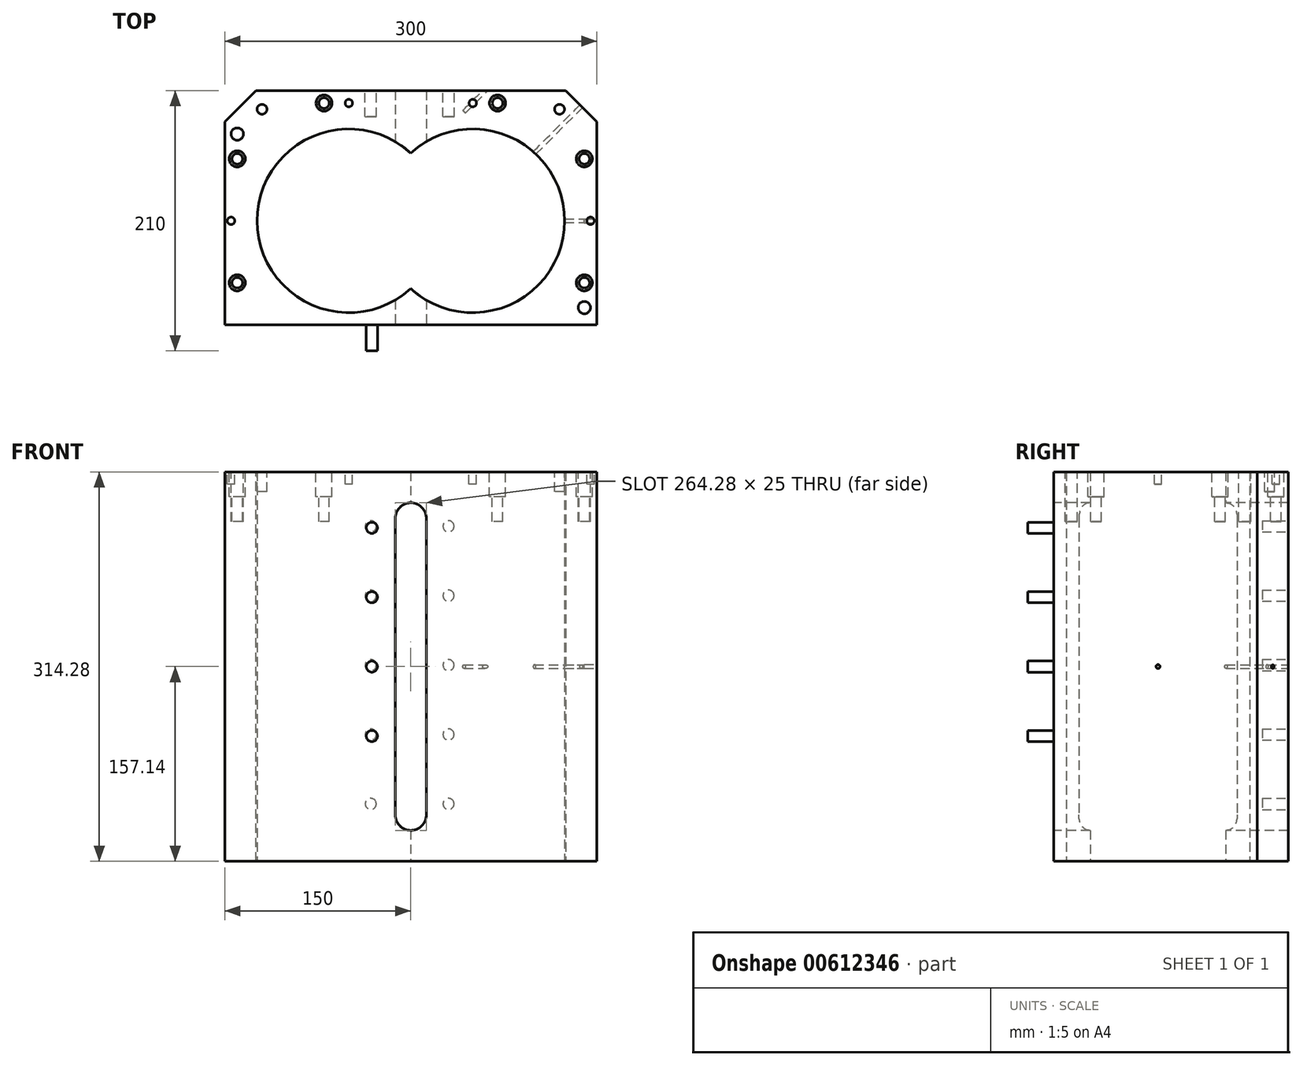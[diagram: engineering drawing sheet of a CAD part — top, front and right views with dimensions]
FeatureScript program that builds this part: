
annotation { "Feature Type Name" : "Feature", "Feature Type Description" : "" }
export const myFeature = defineFeature(function(context is Context, id is Id, definition is map)
    precondition{}
    {
        {
            var Q0;
            Q0=qCreatedBy(makeId("Top.planeOp"),FACE);
            var sketch = newSketch(context, id + "F0", { "sketchPlane" : qUnion([Q0])});
            skLineSegment(sketch, "E0.top", {"start": v(-150, 105) * mm, "end": v(150, 105) * mm});
            skLineSegment(sketch, "E0.right", {"start": v(150, -105) * mm, "end": v(150, 105) * mm});
            skArc(sketch, "E1", {"start": v(-50, 81) * mm, "mid": v(-131, 0) * mm, "end": v(-50, -81) * mm});
            skArc(sketch, "E2", {"start": v(50, -81) * mm, "mid": v(131, 0) * mm, "end": v(50, 81) * mm});
            skArc(sketch, "E3", {"start": v(-50, 86) * mm, "mid": v(-136, 0) * mm, "end": v(-50, -86) * mm});
            skArc(sketch, "E4", {"start": v(0, 54.66) * mm, "mid": v(-124.08, 0) * mm, "end": v(0, -54.66) * mm});
            skArc(sketch, "E5", {"start": v(50, -86) * mm, "mid": v(136, 0) * mm, "end": v(50, 86) * mm});
            skArc(sketch, "E6", {"start": v(0, -54.66) * mm, "mid": v(124.08, 0) * mm, "end": v(0, 54.66) * mm});
            skLineSegment(sketch, "E7", {"start": v(-50, -81) * mm, "end": v(50, -81) * mm});
            skLineSegment(sketch, "E8", {"start": v(-50, 81) * mm, "end": v(50, 81) * mm});
            skLineSegment(sketch, "E9", {"start": v(-50, 86) * mm, "end": v(50, 86) * mm});
            skLineSegment(sketch, "E10", {"start": v(50, -86) * mm, "end": v(-50, -86) * mm});
            skLineSegment(sketch, "E11", {"start": v(-150, 105) * mm, "end": v(-150, -105) * mm});
            skLineSegment(sketch, "E12", {"start": v(-150, -105) * mm, "end": v(150, -105) * mm});
            skSolve(sketch);
        }
        {
            var Q0;
            Q0=makeQuery(id+"F0.imprint","IMPRINT",FACE,{"disambiguationData":[TD([[makeQuery(id+"F0.imprint","IMPRINT",EDGE,{"derivedFrom":sQuery(id+"F0.wireOp",EDGE,"E0.top")}),-1.0]])]});
            var Q1;
            Q1=makeQuery(id+"F0.imprint","IMPRINT",FACE,{"disambiguationData":[TD([[makeQuery(id+"F0.imprint","IMPRINT",EDGE,{"derivedFrom":sQuery(id+"F0.wireOp",EDGE,"E1")}),-1.0]])]});
            var Q2;
            Q2=makeQuery(id+"F0.imprint","IMPRINT",FACE,{"disambiguationData":[TD([[makeQuery(id+"F0.imprint","IMPRINT",EDGE,{"derivedFrom":sQuery(id+"F0.wireOp",EDGE,"E1")}),1.0]])]});
            extrude(context, id + "F1", {"entities" : qUnion([Q0, Q1, Q2]), "depth" : 157.14 * mm, "offsetDistance" : 25 * mm, "hasSecondDirection" : true, "secondDirectionOppositeDirection" : true, "secondDirectionDepth" : 157.14 * mm});
        }
        {
            var Q0;
            Q0=qCreatedBy(makeId("Front.planeOp"),FACE);
            var sketch = newSketch(context, id + "F2", { "sketchPlane" : qUnion([Q0])});
            skLineSegment(sketch, "E13.left", {"start": v(-12.5, 119.64) * mm, "end": v(-12.5, -119.64) * mm});
            skLineSegment(sketch, "E13.right", {"start": v(12.5, 119.64) * mm, "end": v(12.5, -119.64) * mm});
            skArc(sketch, "E14", {"start": v(12.5, 119.64) * mm, "mid": v(0, 132.14) * mm, "end": v(-12.5, 119.64) * mm});
            skArc(sketch, "E15", {"start": v(-12.5, -119.64) * mm, "mid": v(0, -132.14) * mm, "end": v(12.5, -119.64) * mm});
            skSolve(sketch);
        }
        {
            var Q0;
            Q0=makeQuery(id+"F2.imprint","IMPRINT",FACE,{"disambiguationData":[TD([[makeQuery(id+"F2.imprint","IMPRINT",EDGE,{"derivedFrom":sQuery(id+"F2.wireOp",EDGE,"E13.left")}),1.0]])]});
            extrude(context, id + "F3", {"entities" : qUnion([Q0]), "operationType" : NewBodyOperationType.REMOVE, "oppositeDirection" : true, "depth" : 105 * mm, "offsetDistance" : 25 * mm, "hasSecondDirection" : true, "secondDirectionOppositeDirection" : false, "secondDirectionDepth" : 105 * mm});
        }
        {
            var Q0;
            Q0=makeQuery(id+"F1.opExtrude","SWEPT_FACE",FACE,{"disambiguationData":[OSD([sQuery(id+"F0.wireOp",EDGE,"E12")])]});
            var sketch = newSketch(context, id + "F4", { "sketchPlane" : qUnion([Q0])});
            skCircle(sketch, "E16", {"center": v(31.4, -112) * mm, "radius": 4.5 * mm});
            skCircle(sketch, "E17.3.0", {"center": v(-31.4, -112) * mm, "radius": 4.5 * mm});
            skCircle(sketch, "E18", {"center": v(31.4, -56) * mm, "radius": 4.5 * mm});
            skCircle(sketch, "E19", {"center": v(31.4, 0) * mm, "radius": 4.5 * mm});
            skCircle(sketch, "E20", {"center": v(31.4, 56) * mm, "radius": 4.5 * mm});
            skCircle(sketch, "E21", {"center": v(31.4, 112) * mm, "radius": 4.5 * mm});
            skCircle(sketch, "E22.MirrorC", {"center": v(-31.4, 112) * mm, "radius": 4.5 * mm});
            skCircle(sketch, "E23.MirrorC", {"center": v(-31.4, 56) * mm, "radius": 4.5 * mm});
            skCircle(sketch, "E24.MirrorC", {"center": v(-31.4, 0) * mm, "radius": 4.5 * mm});
            skCircle(sketch, "E25.MirrorC", {"center": v(-31.4, -56) * mm, "radius": 4.5 * mm});
            skSolve(sketch);
        }
        {
            var Q0;
            Q0=makeQuery(id+"F4.imprint","IMPRINT",FACE,{"disambiguationData":[TD([[makeQuery(id+"F4.imprint","IMPRINT",EDGE,{"derivedFrom":sQuery(id+"F4.wireOp",EDGE,"d7dd9468-2d27-4aad-933e-c1cbb9862e0e0.MirrorC")}),-1.0]])]});
            var Q1;
            Q1=makeQuery(id+"F4.imprint","IMPRINT",FACE,{"disambiguationData":[TD([[makeQuery(id+"F4.imprint","IMPRINT",EDGE,{"derivedFrom":sQuery(id+"F4.wireOp",EDGE,"e4527831-351d-4cbc-a9db-844e189b8d3e0.MirrorC")}),-1.0]])]});
            var Q2;
            Q2=makeQuery(id+"F4.imprint","IMPRINT",FACE,{"disambiguationData":[TD([[makeQuery(id+"F4.imprint","IMPRINT",EDGE,{"derivedFrom":sQuery(id+"F4.wireOp",EDGE,"fd657ee0-c63a-4506-9bfe-7fd184a3cc340.MirrorC")}),-1.0]])]});
            var Q3;
            Q3=makeQuery(id+"F4.imprint","IMPRINT",FACE,{"disambiguationData":[TD([[makeQuery(id+"F4.imprint","IMPRINT",EDGE,{"derivedFrom":sQuery(id+"F4.wireOp",EDGE,"E22.MirrorC")}),-1.0]])]});
            var Q4;
            Q4=makeQuery(id+"F4.imprint","IMPRINT",FACE,{"disambiguationData":[TD([[makeQuery(id+"F4.imprint","IMPRINT",EDGE,{"derivedFrom":sQuery(id+"F4.wireOp",EDGE,"E23.MirrorC")}),-1.0]])]});
            var Q5;
            Q5=makeQuery(id+"F4.imprint","IMPRINT",FACE,{"disambiguationData":[TD([[makeQuery(id+"F4.imprint","IMPRINT",EDGE,{"derivedFrom":sQuery(id+"F4.wireOp",EDGE,"E24.MirrorC")}),-1.0]])]});
            var Q6;
            Q6=makeQuery(id+"F4.imprint","IMPRINT",FACE,{"disambiguationData":[TD([[makeQuery(id+"F4.imprint","IMPRINT",EDGE,{"derivedFrom":sQuery(id+"F4.wireOp",EDGE,"E25.MirrorC")}),-1.0]])]});
            var Q7;
            Q7=makeQuery(id+"F4.imprint","IMPRINT",FACE,{"disambiguationData":[TD([[makeQuery(id+"F4.imprint","IMPRINT",EDGE,{"derivedFrom":sQuery(id+"F4.wireOp",EDGE,"E17.3.0")}),1.0]])]});
            var Q8;
            Q8=makeQuery(id+"F4.imprint","IMPRINT",FACE,{"disambiguationData":[TD([[makeQuery(id+"F4.imprint","IMPRINT",EDGE,{"derivedFrom":sQuery(id+"F4.wireOp",EDGE,"E16")}),1.0]])]});
            var Q9;
            Q9=makeQuery(id+"F4.imprint","IMPRINT",FACE,{"disambiguationData":[TD([[makeQuery(id+"F4.imprint","IMPRINT",EDGE,{"derivedFrom":sQuery(id+"F4.wireOp",EDGE,"E18")}),1.0]])]});
            var Q10;
            Q10=makeQuery(id+"F4.imprint","IMPRINT",FACE,{"disambiguationData":[TD([[makeQuery(id+"F4.imprint","IMPRINT",EDGE,{"derivedFrom":sQuery(id+"F4.wireOp",EDGE,"E19")}),1.0]])]});
            var Q11;
            Q11=makeQuery(id+"F4.imprint","IMPRINT",FACE,{"disambiguationData":[TD([[makeQuery(id+"F4.imprint","IMPRINT",EDGE,{"derivedFrom":sQuery(id+"F4.wireOp",EDGE,"E20")}),1.0]])]});
            var Q12;
            Q12=makeQuery(id+"F4.imprint","IMPRINT",FACE,{"disambiguationData":[TD([[makeQuery(id+"F4.imprint","IMPRINT",EDGE,{"derivedFrom":sQuery(id+"F4.wireOp",EDGE,"E21")}),1.0]])]});
            var Q13;
            Q13=makeQuery(id+"F4.imprint","IMPRINT",FACE,{"disambiguationData":[TD([[makeQuery(id+"F4.imprint","IMPRINT",EDGE,{"derivedFrom":sQuery(id+"F4.wireOp",EDGE,"9xouMa0X-Z2gg-Zd0Z-shEU-6vQGR6SH1V26")}),1.0]])]});
            var Q14;
            Q14=makeQuery(id+"F4.imprint","IMPRINT",FACE,{"disambiguationData":[TD([[makeQuery(id+"F4.imprint","IMPRINT",EDGE,{"derivedFrom":sQuery(id+"F4.wireOp",EDGE,"f3L94pXb-UXOi-ypgG-wCGD-cI5cRXITr2G3")}),1.0]])]});
            var Q15;
            Q15=makeQuery(id+"F4.imprint","IMPRINT",FACE,{"disambiguationData":[TD([[makeQuery(id+"F4.imprint","IMPRINT",EDGE,{"derivedFrom":sQuery(id+"F4.wireOp",EDGE,"yZ0yZw9I-iKcT-nnKl-4C5n-boTp4ZFd5wa9")}),1.0]])]});
            extrude(context, id + "F5", {"entities" : qUnion([Q0, Q1, Q2, Q3, Q4, Q5, Q6, Q7, Q8, Q9, Q10, Q11, Q12, Q13, Q14, Q15]), "operationType" : NewBodyOperationType.REMOVE, "oppositeDirection" : true, "depth" : 21 * mm, "offsetDistance" : 25 * mm});
        }
        {
            var Q0;
            Q0=makeQuery(id+"F1.opExtrude","CAP_FACE",FACE,{"disambiguationData":[OSD([sQuery(id+"F0.wireOp",EDGE,"E0.top"),sQuery(id+"F0.wireOp",EDGE,"E0.right"),sQuery(id+"F0.wireOp",EDGE,"E3"),sQuery(id+"F0.wireOp",EDGE,"E5"),sQuery(id+"F0.wireOp",EDGE,"E9"),sQuery(id+"F0.wireOp",EDGE,"E10"),sQuery(id+"F0.wireOp",EDGE,"E11"),sQuery(id+"F0.wireOp",EDGE,"E12")])],"isStart":false});
            var sketch = newSketch(context, id + "F6", { "sketchPlane" : qUnion([Q0])});
            skCircle(sketch, "E26", {"center": v(-70, 95) * mm, "radius": 6.5 * mm});
            skCircle(sketch, "E27", {"center": v(70, 95) * mm, "radius": 6.5 * mm});
            skCircle(sketch, "E28", {"center": v(70, -95) * mm, "radius": 6.5 * mm});
            skCircle(sketch, "E29", {"center": v(-70, -95) * mm, "radius": 6.5 * mm});
            skCircle(sketch, "E30", {"center": v(-140, -50) * mm, "radius": 6.5 * mm});
            skCircle(sketch, "E31", {"center": v(-140, 50) * mm, "radius": 6.5 * mm});
            skCircle(sketch, "E32", {"center": v(140, 50) * mm, "radius": 6.5 * mm});
            skCircle(sketch, "E33", {"center": v(140, -50) * mm, "radius": 6.5 * mm});
            skCircle(sketch, "E34", {"center": v(-140, 70) * mm, "radius": 5 * mm});
            skCircle(sketch, "E35", {"center": v(140, -70) * mm, "radius": 5 * mm});
            skCircle(sketch, "E36", {"center": v(-145, 0) * mm, "radius": 3 * mm});
            skCircle(sketch, "E37", {"center": v(145, 0) * mm, "radius": 3 * mm});
            skCircle(sketch, "E38", {"center": v(50, -95) * mm, "radius": 3 * mm});
            skCircle(sketch, "E39", {"center": v(-50, -95) * mm, "radius": 3 * mm});
            skCircle(sketch, "E40", {"center": v(-50, 95) * mm, "radius": 3 * mm});
            skCircle(sketch, "E41", {"center": v(50, 95) * mm, "radius": 3 * mm});
            skCircle(sketch, "E42", {"center": v(-120, 90) * mm, "radius": 4 * mm});
            skCircle(sketch, "E43", {"center": v(-120, -90) * mm, "radius": 4 * mm});
            skCircle(sketch, "E44", {"center": v(120, -90) * mm, "radius": 4 * mm});
            skCircle(sketch, "E45", {"center": v(120, 90) * mm, "radius": 4 * mm});
            skCircle(sketch, "E46", {"center": v(-70, 95) * mm, "radius": 4.25 * mm});
            skCircle(sketch, "E47", {"center": v(70, 95) * mm, "radius": 4.25 * mm});
            skCircle(sketch, "E48", {"center": v(140, 50) * mm, "radius": 4.25 * mm});
            skCircle(sketch, "E49", {"center": v(140, -50) * mm, "radius": 4.25 * mm});
            skCircle(sketch, "E50", {"center": v(70, -95) * mm, "radius": 4.25 * mm});
            skCircle(sketch, "E51", {"center": v(-70, -95) * mm, "radius": 4.25 * mm});
            skCircle(sketch, "E52", {"center": v(-140, -50) * mm, "radius": 4.25 * mm});
            skCircle(sketch, "E53", {"center": v(-140, 50) * mm, "radius": 4.25 * mm});
            skSolve(sketch);
        }
        {
            var Q0;
            Q0=makeQuery(id+"F6.imprint","IMPRINT",FACE,{"disambiguationData":[TD([[makeQuery(id+"F6.imprint","IMPRINT",EDGE,{"derivedFrom":sQuery(id+"F6.wireOp",EDGE,"E32")}),1.0]])]});
            var Q1;
            Q1=makeQuery(id+"F6.imprint","IMPRINT",FACE,{"disambiguationData":[TD([[makeQuery(id+"F6.imprint","IMPRINT",EDGE,{"derivedFrom":sQuery(id+"F6.wireOp",EDGE,"E33")}),1.0]])]});
            var Q2;
            Q2=makeQuery(id+"F6.imprint","IMPRINT",FACE,{"disambiguationData":[TD([[makeQuery(id+"F6.imprint","IMPRINT",EDGE,{"derivedFrom":sQuery(id+"F6.wireOp",EDGE,"E28")}),1.0]])]});
            var Q3;
            Q3=makeQuery(id+"F6.imprint","IMPRINT",FACE,{"disambiguationData":[TD([[makeQuery(id+"F6.imprint","IMPRINT",EDGE,{"derivedFrom":sQuery(id+"F6.wireOp",EDGE,"E29")}),1.0]])]});
            var Q4;
            Q4=makeQuery(id+"F6.imprint","IMPRINT",FACE,{"disambiguationData":[TD([[makeQuery(id+"F6.imprint","IMPRINT",EDGE,{"derivedFrom":sQuery(id+"F6.wireOp",EDGE,"E30")}),1.0]])]});
            var Q5;
            Q5=makeQuery(id+"F6.imprint","IMPRINT",FACE,{"disambiguationData":[TD([[makeQuery(id+"F6.imprint","IMPRINT",EDGE,{"derivedFrom":sQuery(id+"F6.wireOp",EDGE,"E31")}),1.0]])]});
            var Q6;
            Q6=makeQuery(id+"F6.imprint","IMPRINT",FACE,{"disambiguationData":[TD([[makeQuery(id+"F6.imprint","IMPRINT",EDGE,{"derivedFrom":sQuery(id+"F6.wireOp",EDGE,"E26")}),1.0]])]});
            var Q7;
            Q7=makeQuery(id+"F6.imprint","IMPRINT",FACE,{"disambiguationData":[TD([[makeQuery(id+"F6.imprint","IMPRINT",EDGE,{"derivedFrom":sQuery(id+"F6.wireOp",EDGE,"E27")}),1.0]])]});
            extrude(context, id + "F7", {"entities" : qUnion([Q0, Q1, Q2, Q3, Q4, Q5, Q6, Q7]), "operationType" : NewBodyOperationType.REMOVE, "oppositeDirection" : true, "depth" : 20 * mm, "offsetDistance" : 25 * mm});
        }
        {
            var Q0;
            Q0=makeQuery(id+"F6.imprint","IMPRINT",FACE,{"disambiguationData":[TD([[makeQuery(id+"F6.imprint","IMPRINT",EDGE,{"derivedFrom":sQuery(id+"F6.wireOp",EDGE,"E40")}),1.0]])]});
            var Q1;
            Q1=makeQuery(id+"F6.imprint","IMPRINT",FACE,{"disambiguationData":[TD([[makeQuery(id+"F6.imprint","IMPRINT",EDGE,{"derivedFrom":sQuery(id+"F6.wireOp",EDGE,"E36")}),1.0]])]});
            var Q2;
            Q2=makeQuery(id+"F6.imprint","IMPRINT",FACE,{"disambiguationData":[TD([[makeQuery(id+"F6.imprint","IMPRINT",EDGE,{"derivedFrom":sQuery(id+"F6.wireOp",EDGE,"E41")}),1.0]])]});
            var Q3;
            Q3=makeQuery(id+"F6.imprint","IMPRINT",FACE,{"disambiguationData":[TD([[makeQuery(id+"F6.imprint","IMPRINT",EDGE,{"derivedFrom":sQuery(id+"F6.wireOp",EDGE,"E37")}),1.0]])]});
            var Q4;
            Q4=makeQuery(id+"F6.imprint","IMPRINT",FACE,{"disambiguationData":[TD([[makeQuery(id+"F6.imprint","IMPRINT",EDGE,{"derivedFrom":sQuery(id+"F6.wireOp",EDGE,"E39")}),1.0]])]});
            var Q5;
            Q5=makeQuery(id+"F6.imprint","IMPRINT",FACE,{"disambiguationData":[TD([[makeQuery(id+"F6.imprint","IMPRINT",EDGE,{"derivedFrom":sQuery(id+"F6.wireOp",EDGE,"E38")}),1.0]])]});
            extrude(context, id + "F8", {"entities" : qUnion([Q0, Q1, Q2, Q3, Q4, Q5]), "operationType" : NewBodyOperationType.REMOVE, "oppositeDirection" : true, "depth" : 10 * mm, "offsetDistance" : 25 * mm});
        }
        {
            var Q0;
            Q0=makeQuery(id+"F6.imprint","IMPRINT",FACE,{"disambiguationData":[TD([[makeQuery(id+"F6.imprint","IMPRINT",EDGE,{"derivedFrom":sQuery(id+"F6.wireOp",EDGE,"E46")}),1.0]])]});
            var Q1;
            Q1=makeQuery(id+"F6.imprint","IMPRINT",FACE,{"disambiguationData":[TD([[makeQuery(id+"F6.imprint","IMPRINT",EDGE,{"derivedFrom":sQuery(id+"F6.wireOp",EDGE,"E53")}),1.0]])]});
            var Q2;
            Q2=makeQuery(id+"F6.imprint","IMPRINT",FACE,{"disambiguationData":[TD([[makeQuery(id+"F6.imprint","IMPRINT",EDGE,{"derivedFrom":sQuery(id+"F6.wireOp",EDGE,"E52")}),1.0]])]});
            var Q3;
            Q3=makeQuery(id+"F6.imprint","IMPRINT",FACE,{"disambiguationData":[TD([[makeQuery(id+"F6.imprint","IMPRINT",EDGE,{"derivedFrom":sQuery(id+"F6.wireOp",EDGE,"E51")}),1.0]])]});
            var Q4;
            Q4=makeQuery(id+"F6.imprint","IMPRINT",FACE,{"disambiguationData":[TD([[makeQuery(id+"F6.imprint","IMPRINT",EDGE,{"derivedFrom":sQuery(id+"F6.wireOp",EDGE,"E50")}),1.0]])]});
            var Q5;
            Q5=makeQuery(id+"F6.imprint","IMPRINT",FACE,{"disambiguationData":[TD([[makeQuery(id+"F6.imprint","IMPRINT",EDGE,{"derivedFrom":sQuery(id+"F6.wireOp",EDGE,"E49")}),1.0]])]});
            var Q6;
            Q6=makeQuery(id+"F6.imprint","IMPRINT",FACE,{"disambiguationData":[TD([[makeQuery(id+"F6.imprint","IMPRINT",EDGE,{"derivedFrom":sQuery(id+"F6.wireOp",EDGE,"E48")}),1.0]])]});
            var Q7;
            Q7=makeQuery(id+"F6.imprint","IMPRINT",FACE,{"disambiguationData":[TD([[makeQuery(id+"F6.imprint","IMPRINT",EDGE,{"derivedFrom":sQuery(id+"F6.wireOp",EDGE,"E47")}),1.0]])]});
            var Q8;
            Q8=makeQuery(id+"F6.imprint","IMPRINT",FACE,{"disambiguationData":[TD([[makeQuery(id+"F6.imprint","IMPRINT",EDGE,{"derivedFrom":sQuery(id+"F6.wireOp",EDGE,"E34")}),1.0]])]});
            var Q9;
            Q9=makeQuery(id+"F6.imprint","IMPRINT",FACE,{"disambiguationData":[TD([[makeQuery(id+"F6.imprint","IMPRINT",EDGE,{"derivedFrom":sQuery(id+"F6.wireOp",EDGE,"E35")}),1.0]])]});
            extrude(context, id + "F9", {"entities" : qUnion([Q0, Q1, Q2, Q3, Q4, Q5, Q6, Q7, Q8, Q9]), "operationType" : NewBodyOperationType.REMOVE, "oppositeDirection" : true, "depth" : 40 * mm, "offsetDistance" : 25 * mm});
        }
        {
            var Q0;
            Q0=makeQuery(id+"F6.imprint","IMPRINT",FACE,{"disambiguationData":[TD([[makeQuery(id+"F6.imprint","IMPRINT",EDGE,{"derivedFrom":sQuery(id+"F6.wireOp",EDGE,"E42")}),1.0]])]});
            var Q1;
            Q1=makeQuery(id+"F6.imprint","IMPRINT",FACE,{"disambiguationData":[TD([[makeQuery(id+"F6.imprint","IMPRINT",EDGE,{"derivedFrom":sQuery(id+"F6.wireOp",EDGE,"E43")}),1.0]])]});
            var Q2;
            Q2=makeQuery(id+"F6.imprint","IMPRINT",FACE,{"disambiguationData":[TD([[makeQuery(id+"F6.imprint","IMPRINT",EDGE,{"derivedFrom":sQuery(id+"F6.wireOp",EDGE,"E44")}),1.0]])]});
            var Q3;
            Q3=makeQuery(id+"F6.imprint","IMPRINT",FACE,{"disambiguationData":[TD([[makeQuery(id+"F6.imprint","IMPRINT",EDGE,{"derivedFrom":sQuery(id+"F6.wireOp",EDGE,"E45")}),1.0]])]});
            extrude(context, id + "F10", {"entities" : qUnion([Q0, Q1, Q2, Q3]), "operationType" : NewBodyOperationType.REMOVE, "oppositeDirection" : true, "depth" : 16 * mm, "offsetDistance" : 25 * mm});
        }
        {
            var Q0;
            Q0=makeQuery(id+"F1.opExtrude","SWEPT_EDGE",EDGE,{"disambiguationData":[OSD([sQuery(id+"F0.wireOp",EDGE,"E0.top"),sQuery(id+"F0.wireOp",EDGE,"E11")])]});
            var Q1;
            Q1=makeQuery(id+"F1.opExtrude","SWEPT_EDGE",EDGE,{"disambiguationData":[OSD([sQuery(id+"F0.wireOp",EDGE,"E11"),sQuery(id+"F0.wireOp",EDGE,"E12")])]});
            var Q2;
            Q2=makeQuery(id+"F1.opExtrude","SWEPT_EDGE",EDGE,{"disambiguationData":[OSD([sQuery(id+"F0.wireOp",EDGE,"E0.top"),sQuery(id+"F0.wireOp",EDGE,"E0.right")])]});
            var Q3;
            Q3=makeQuery(id+"F1.opExtrude","SWEPT_EDGE",EDGE,{"disambiguationData":[OSD([sQuery(id+"F0.wireOp",EDGE,"E0.right"),sQuery(id+"F0.wireOp",EDGE,"E12")])]});
            chamfer(context, id + "F11", {"entities" : qUnion([Q0, Q1, Q2, Q3]), "width" : 25 * mm, "tangentPropagation" : true});
        }
        {
            var Q0;
            Q0=makeQuery(id+"F1.opExtrude","SWEPT_FACE",FACE,{"disambiguationData":[OSD([sQuery(id+"F0.wireOp",EDGE,"E0.right")])]});
            var sketch = newSketch(context, id + "F12", { "sketchPlane" : qUnion([Q0])});
            skCircle(sketch, "E54", {"center": v(0, 0) * mm, "radius": 1.59 * mm});
            skCircle(sketch, "E55", {"center": v(0, 0) * mm, "radius": 1.5 * mm});
            skSolve(sketch);
        }
        {
            var Q0;
            Q0=makeQuery(id+"F12.imprint","IMPRINT",FACE,{"disambiguationData":[TD([[makeQuery(id+"F12.imprint","IMPRINT",EDGE,{"derivedFrom":sQuery(id+"F12.wireOp",EDGE,"E54")}),1.0]])]});
            extrude(context, id + "F13", {"entities" : qUnion([Q0]), "operationType" : NewBodyOperationType.REMOVE, "oppositeDirection" : true, "depth" : 10 * mm, "offsetDistance" : 25 * mm});
        }
        {
            var Q0;
            Q0=makeQuery(id+"F13.boolean.opBoolean","SPLIT",FACE,{"disambiguationData":[TD([makeQuery(id+"F13.opExtrude","SWEPT_FACE",FACE,{"disambiguationData":[OSD([sQuery(id+"F12.wireOp",EDGE,"E55")])]})])],"derivedFrom":makeQuery(id+"F1.opExtrude","SWEPT_FACE",FACE,{"disambiguationData":[OSD([sQuery(id+"F0.wireOp",EDGE,"E0.right")])]})});
            extrude(context, id + "F14", {"entities" : qUnion([Q0]), "operationType" : NewBodyOperationType.REMOVE, "oppositeDirection" : true, "depth" : 40 * mm, "offsetDistance" : 25 * mm});
        }
        {
            var Q0;
            Q0=makeQuery(id+"F11.opChamfer","BLEND_FACE",FACE,{"disambiguationData":[OSD([sQuery(id+"F0.wireOp",EDGE,"E0.right"),sQuery(id+"F0.wireOp",EDGE,"E12")])]});
            var sketch = newSketch(context, id + "F15", { "sketchPlane" : qUnion([Q0])});
            skCircle(sketch, "E56", {"center": v(31.82, 0) * mm, "radius": 1.59 * mm});
            skCircle(sketch, "E57", {"center": v(31.82, 0) * mm, "radius": 1.5 * mm});
            skSolve(sketch);
        }
        {
            var Q0;
            Q0=makeQuery(id+"F15.imprint","IMPRINT",FACE,{"disambiguationData":[TD([[makeQuery(id+"F15.imprint","IMPRINT",EDGE,{"derivedFrom":sQuery(id+"F15.wireOp",EDGE,"E57")}),1.0]])]});
            extrude(context, id + "F16", {"entities" : qUnion([Q0]), "operationType" : NewBodyOperationType.REMOVE, "oppositeDirection" : true, "depth" : 70 * mm, "offsetDistance" : 25 * mm});
        }
        {
            var Q0;
            Q0=makeQuery(id+"F11.opChamfer","BLEND_FACE",FACE,{"disambiguationData":[OSD([sQuery(id+"F0.wireOp",EDGE,"E0.top"),sQuery(id+"F0.wireOp",EDGE,"E0.right")])]});
            var sketch = newSketch(context, id + "F17", { "sketchPlane" : qUnion([Q0])});
            skCircle(sketch, "E58", {"center": v(-31.82, 0) * mm, "radius": 1.59 * mm});
            skCircle(sketch, "E59", {"center": v(-31.82, 0) * mm, "radius": 1.5 * mm});
            skSolve(sketch);
        }
        {
            var Q0;
            Q0=makeQuery(id+"F17.imprint","IMPRINT",FACE,{"disambiguationData":[TD([[makeQuery(id+"F17.imprint","IMPRINT",EDGE,{"derivedFrom":sQuery(id+"F17.wireOp",EDGE,"E59")}),1.0]])]});
            extrude(context, id + "F18", {"entities" : qUnion([Q0]), "operationType" : NewBodyOperationType.REMOVE, "oppositeDirection" : true, "depth" : 70 * mm, "offsetDistance" : 25 * mm});
        }
        {
            var Q0;
            {var subQ0=sQuery(id+"F0.wireOp",EDGE,"E0.top");var subQ1=sQuery(id+"F0.wireOp",EDGE,"E12");var subQ2=sQuery(id+"F0.wireOp",EDGE,"E11");var subQ3=sQuery(id+"F0.wireOp",EDGE,"E0.right");var subQ4=sQuery(id+"F0.wireOp",EDGE,"E6");var subQ5=sQuery(id+"F0.wireOp",EDGE,"E4");Q0=makeQuery(id+"F7.boolean.opBoolean","SPLIT",FACE,{"disambiguationData":[TD([makeQuery(id+"F1.opExtrude","SWEPT_FACE",FACE,{"disambiguationData":[OSD([subQ0])]})])],"derivedFrom":makeQuery(id+"F1.opExtrude","CAP_FACE",FACE,{"disambiguationData":[OSD([subQ0,subQ3,subQ5,subQ4,subQ2,subQ1])],"isStart":false})});}
            var sketch = newSketch(context, id + "F19", { "sketchPlane" : qUnion([Q0])});
            skArc(sketch, "E60", {"start": v(50, -86) * mm, "mid": v(136, 0) * mm, "end": v(50, 86) * mm});
            skArc(sketch, "E61", {"start": v(50, -81) * mm, "mid": v(131, 0) * mm, "end": v(50, 81) * mm});
            skArc(sketch, "E62", {"start": v(-50, 86) * mm, "mid": v(-136, 0) * mm, "end": v(-50, -86) * mm});
            skArc(sketch, "E63", {"start": v(-50, 81) * mm, "mid": v(-131, 0) * mm, "end": v(-50, -81) * mm});
            skLineSegment(sketch, "E64", {"start": v(-50, 86) * mm, "end": v(50, 86) * mm});
            skLineSegment(sketch, "E65", {"start": v(50, 81) * mm, "end": v(-50, 81) * mm});
            skLineSegment(sketch, "E66", {"start": v(-50, -81) * mm, "end": v(50, -81) * mm});
            skLineSegment(sketch, "E67", {"start": v(50, -86) * mm, "end": v(-50, -86) * mm});
            skSolve(sketch);
        }
        {
            var Q0;
            Q0=makeQuery(id+"F19.imprint","IMPRINT",FACE,{"disambiguationData":[TD([[makeQuery(id+"F19.imprint","IMPRINT",EDGE,{"derivedFrom":sQuery(id+"F19.wireOp",EDGE,"E60")}),1.0]])]});
            extrude(context, id + "F20", {"entities" : qUnion([Q0]), "operationType" : NewBodyOperationType.REMOVE, "oppositeDirection" : true, "depth" : 2.7 * mm, "offsetDistance" : 25 * mm});
        }
        {
            var Q0;
            Q0=makeQuery(id+"F1.opExtrude","CAP_FACE",FACE,{"disambiguationData":[OSD([sQuery(id+"F0.wireOp",EDGE,"E0.top"),sQuery(id+"F0.wireOp",EDGE,"E0.right"),sQuery(id+"F0.wireOp",EDGE,"E4"),sQuery(id+"F0.wireOp",EDGE,"E6"),sQuery(id+"F0.wireOp",EDGE,"E11"),sQuery(id+"F0.wireOp",EDGE,"E12")])],"isStart":true});
            var sketch = newSketch(context, id + "F21", { "sketchPlane" : qUnion([Q0])});
            skArc(sketch, "E68", {"start": v(-50, 86) * mm, "mid": v(-136, 0) * mm, "end": v(-50, -86) * mm});
            skArc(sketch, "E69", {"start": v(-50, 81) * mm, "mid": v(-131, 0) * mm, "end": v(-50, -81) * mm});
            skArc(sketch, "E70", {"start": v(50, -86) * mm, "mid": v(136, 0) * mm, "end": v(50, 86) * mm});
            skArc(sketch, "E71", {"start": v(50, -81) * mm, "mid": v(131, 0) * mm, "end": v(50, 81) * mm});
            skLineSegment(sketch, "E72", {"start": v(-50, 81) * mm, "end": v(50, 81) * mm});
            skLineSegment(sketch, "E73", {"start": v(50, 86) * mm, "end": v(-50, 86) * mm});
            skLineSegment(sketch, "E74", {"start": v(-50, -81) * mm, "end": v(50, -81) * mm});
            skLineSegment(sketch, "E75", {"start": v(50, -86) * mm, "end": v(-50, -86) * mm});
            skSolve(sketch);
        }
        {
            var Q0;
            Q0=makeQuery(id+"F21.imprint","IMPRINT",FACE,{"disambiguationData":[TD([[makeQuery(id+"F21.imprint","IMPRINT",EDGE,{"derivedFrom":sQuery(id+"F21.wireOp",EDGE,"E68")}),1.0]])]});
            extrude(context, id + "F22", {"entities" : qUnion([Q0]), "operationType" : NewBodyOperationType.REMOVE, "oppositeDirection" : true, "depth" : 2.7 * mm, "offsetDistance" : 25 * mm});
        }
        {
            var Q0;
            Q0=makeQuery(id+"F1.opExtrude","SWEPT_FACE",FACE,{"disambiguationData":[OSD([sQuery(id+"F0.wireOp",EDGE,"E0.top")])]});
            var sketch = newSketch(context, id + "F23", { "sketchPlane" : qUnion([Q0])});
            skCircle(sketch, "E76", {"center": v(32.32, -110.79) * mm, "radius": 4.5 * mm});
            skCircle(sketch, "E77.3.0", {"center": v(-30.48, -110.79) * mm, "radius": 4.5 * mm});
            skCircle(sketch, "E78", {"center": v(32.32, -54.79) * mm, "radius": 4.5 * mm});
            skCircle(sketch, "E79", {"center": v(32.32, 1.21) * mm, "radius": 4.5 * mm});
            skCircle(sketch, "E80", {"center": v(32.32, 57.21) * mm, "radius": 4.5 * mm});
            skCircle(sketch, "E81", {"center": v(32.32, 113.21) * mm, "radius": 4.5 * mm});
            skCircle(sketch, "E82.MirrorC", {"center": v(-30.48, 113.21) * mm, "radius": 4.5 * mm});
            skCircle(sketch, "E83.MirrorC", {"center": v(-30.48, 57.21) * mm, "radius": 4.5 * mm});
            skCircle(sketch, "E84.MirrorC", {"center": v(-30.48, 1.21) * mm, "radius": 4.5 * mm});
            skCircle(sketch, "E85.MirrorC", {"center": v(-30.48, -54.79) * mm, "radius": 4.5 * mm});
            skSolve(sketch);
        }
        {
            var Q0;
            Q0 = qSketchRegion(id + "F23", true);
            extrude(context, id + "F24", {"entities" : qUnion([Q0]), "operationType" : NewBodyOperationType.REMOVE, "oppositeDirection" : true, "depth" : 21 * mm, "offsetDistance" : 25 * mm});
        }
    });
